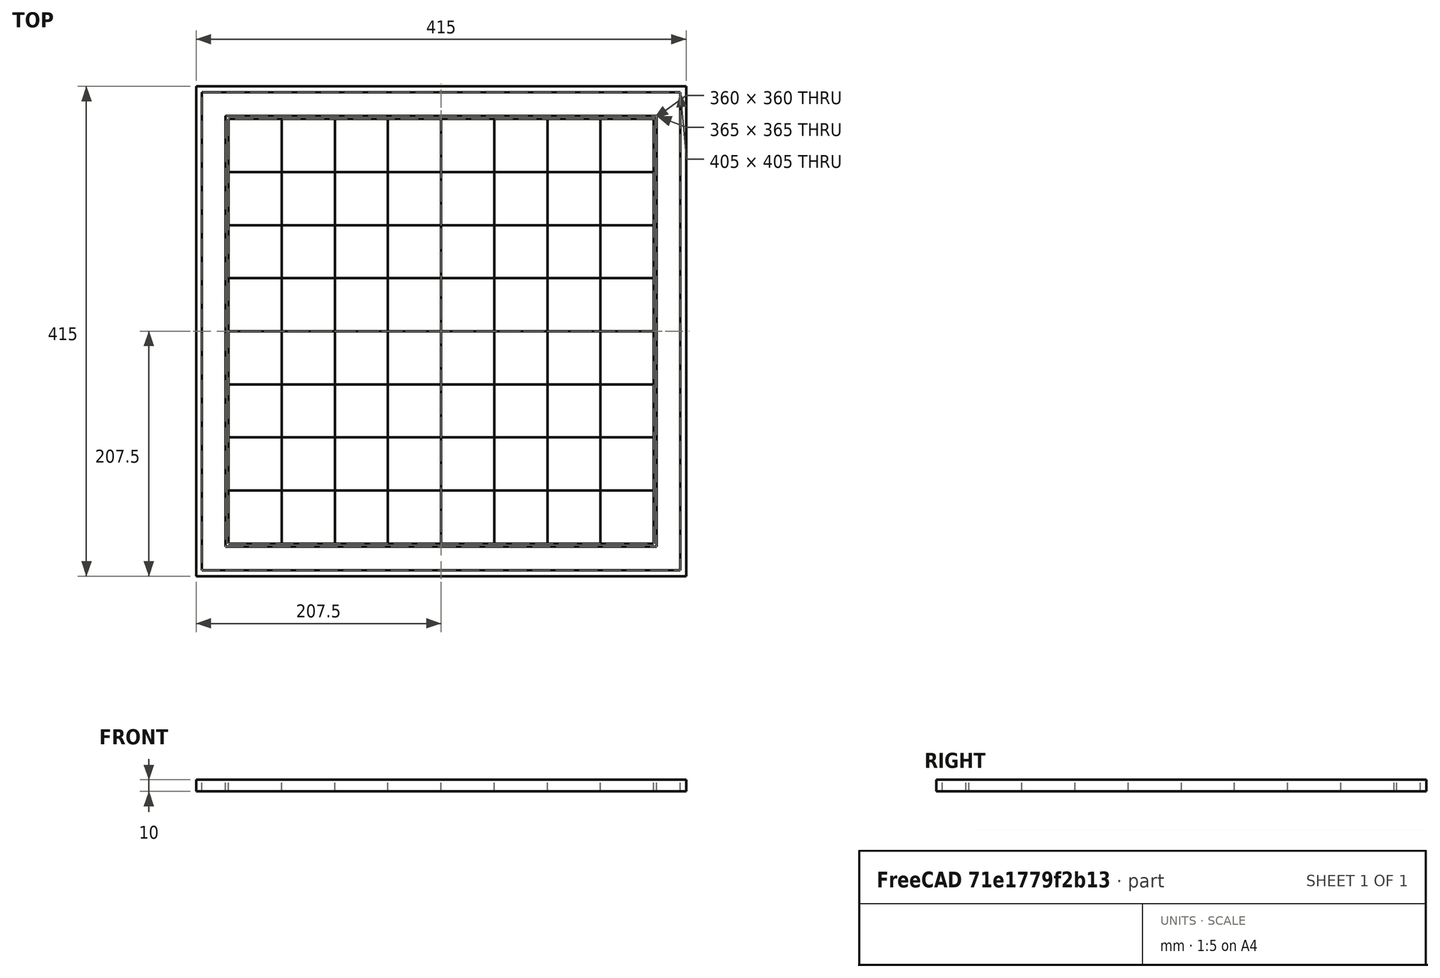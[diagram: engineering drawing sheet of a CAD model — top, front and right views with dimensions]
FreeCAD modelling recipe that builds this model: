
FCSTD DOCUMENT  (FreeCAD 0.20R29410 (Git))
Label: checkersWithCrowns
License: All rights reserved
LicenseURL: http://en.wikipedia.org/wiki/All_rights_reserved
objects: Part::Box×66, Mesh::Feature×48, App::DocumentObjectGroup×13, Sketcher::SketchObject×2, Part::Extrusion×2, Part::Cut×1
note: 71 computed .brp shape members not serialized (recipe doc carries the construction recipe); baked Part::Feature solids carry a one-line shape summary decoded from their .brp

FEATURE [Part::Box] Box  label="A1"
  AttacherType = Attacher::AttachEngine3D
  Height = 10
  Length = 45
  Width = 45
FEATURE [Part::Box] Box001  label="A2"
  AttacherType = Attacher::AttachEngine3D
  Height = 10
  Length = 45
  Placement = pos=(45,0,0) rot=(0,0,1;0rad)
  Width = 45
FEATURE [Part::Box] Box002  label="A3"
  AttacherType = Attacher::AttachEngine3D
  Height = 10
  Length = 45
  Placement = pos=(90,0,0) rot=(0,0,1;0rad)
  Width = 45
FEATURE [Part::Box] Box003  label="A4"
  AttacherType = Attacher::AttachEngine3D
  Height = 10
  Length = 45
  Placement = pos=(135,0,0) rot=(0,0,1;0rad)
  Width = 45
FEATURE [Part::Box] Box004  label="A5"
  AttacherType = Attacher::AttachEngine3D
  Height = 10
  Length = 45
  Placement = pos=(180,0,0) rot=(0,0,1;0rad)
  Width = 45
FEATURE [Part::Box] Box005  label="A6"
  AttacherType = Attacher::AttachEngine3D
  Height = 10
  Length = 45
  Placement = pos=(225,0,0) rot=(0,0,1;0rad)
  Width = 45
FEATURE [Part::Box] Box006  label="A7"
  AttacherType = Attacher::AttachEngine3D
  Height = 10
  Length = 45
  Placement = pos=(270,0,0) rot=(0,0,1;0rad)
  Width = 45
FEATURE [Part::Box] Box007  label="A8"
  AttacherType = Attacher::AttachEngine3D
  Height = 10
  Length = 45
  Placement = pos=(315,0,0) rot=(0,0,1;0rad)
  Width = 45
FEATURE [App::DocumentObjectGroup] Group001  label="A_File"
  Group = -> [Box,Box001,Box002,Box003,Box004,Box005,Box006,Box007]
FEATURE [Part::Box] Box008  label="B1"
  AttacherType = Attacher::AttachEngine3D
  Height = 10
  Length = 45
  Placement = pos=(0,45,0) rot=(0,0,1;0rad)
  Width = 45
FEATURE [Part::Box] Box009  label="B2"
  AttacherType = Attacher::AttachEngine3D
  Height = 10
  Length = 45
  Placement = pos=(45,45,0) rot=(0,0,1;0rad)
  Width = 45
FEATURE [Part::Box] Box010  label="B3"
  AttacherType = Attacher::AttachEngine3D
  Height = 10
  Length = 45
  Placement = pos=(90,45,0) rot=(0,0,1;0rad)
  Width = 45
FEATURE [Part::Box] Box011  label="B4"
  AttacherType = Attacher::AttachEngine3D
  Height = 10
  Length = 45
  Placement = pos=(135,45,0) rot=(0,0,1;0rad)
  Width = 45
FEATURE [Part::Box] Box012  label="B5"
  AttacherType = Attacher::AttachEngine3D
  Height = 10
  Length = 45
  Placement = pos=(180,45,0) rot=(0,0,1;0rad)
  Width = 45
FEATURE [Part::Box] Box013  label="B6"
  AttacherType = Attacher::AttachEngine3D
  Height = 10
  Length = 45
  Placement = pos=(225,45,0) rot=(0,0,1;0rad)
  Width = 45
FEATURE [Part::Box] Box014  label="B7"
  AttacherType = Attacher::AttachEngine3D
  Height = 10
  Length = 45
  Placement = pos=(270,45,0) rot=(0,0,1;0rad)
  Width = 45
FEATURE [Part::Box] Box015  label="B8"
  AttacherType = Attacher::AttachEngine3D
  Height = 10
  Length = 45
  Placement = pos=(315,45,0) rot=(0,0,1;0rad)
  Width = 45
FEATURE [Part::Box] Box016  label="C8"
  AttacherType = Attacher::AttachEngine3D
  Height = 10
  Length = 45
  Placement = pos=(315,90,0) rot=(0,0,1;0rad)
  Width = 45
FEATURE [Part::Box] Box017  label="C7"
  AttacherType = Attacher::AttachEngine3D
  Height = 10
  Length = 45
  Placement = pos=(270,90,0) rot=(0,0,1;0rad)
  Width = 45
FEATURE [Part::Box] Box018  label="C6"
  AttacherType = Attacher::AttachEngine3D
  Height = 10
  Length = 45
  Placement = pos=(225,90,0) rot=(0,0,1;0rad)
  Width = 45
FEATURE [Part::Box] Box019  label="C5"
  AttacherType = Attacher::AttachEngine3D
  Height = 10
  Length = 45
  Placement = pos=(180,90,0) rot=(0,0,1;0rad)
  Width = 45
FEATURE [Part::Box] Box020  label="C4"
  AttacherType = Attacher::AttachEngine3D
  Height = 10
  Length = 45
  Placement = pos=(135,90,0) rot=(0,0,1;0rad)
  Width = 45
FEATURE [Part::Box] Box021  label="C3"
  AttacherType = Attacher::AttachEngine3D
  Height = 10
  Length = 45
  Placement = pos=(90,90,0) rot=(0,0,1;0rad)
  Width = 45
FEATURE [Part::Box] Box022  label="C2"
  AttacherType = Attacher::AttachEngine3D
  Height = 10
  Length = 45
  Placement = pos=(45,90,0) rot=(0,0,1;0rad)
  Width = 45
FEATURE [Part::Box] Box023  label="C1"
  AttacherType = Attacher::AttachEngine3D
  Height = 10
  Length = 45
  Placement = pos=(0,90,0) rot=(0,0,1;0rad)
  Width = 45
FEATURE [App::DocumentObjectGroup] Group002  label="B_File"
  Group = -> [Box008,Box009,Box010,Box011,Box012,Box013,Box014,Box015]
FEATURE [App::DocumentObjectGroup] Group003  label="C_File"
  Group = -> [Box016,Box017,Box018,Box019,Box020,Box021,Box022,Box023]
FEATURE [Part::Box] Box024  label="D8"
  AttacherType = Attacher::AttachEngine3D
  Height = 10
  Length = 45
  Placement = pos=(315,135,0) rot=(0,0,1;0rad)
  Width = 45
FEATURE [Part::Box] Box025  label="D7"
  AttacherType = Attacher::AttachEngine3D
  Height = 10
  Length = 45
  Placement = pos=(270,135,0) rot=(0,0,1;0rad)
  Width = 45
FEATURE [Part::Box] Box026  label="D6"
  AttacherType = Attacher::AttachEngine3D
  Height = 10
  Length = 45
  Placement = pos=(225,135,0) rot=(0,0,1;0rad)
  Width = 45
FEATURE [Part::Box] Box027  label="D5"
  AttacherType = Attacher::AttachEngine3D
  Height = 10
  Length = 45
  Placement = pos=(180,135,0) rot=(0,0,1;0rad)
  Width = 45
FEATURE [Part::Box] Box028  label="D4"
  AttacherType = Attacher::AttachEngine3D
  Height = 10
  Length = 45
  Placement = pos=(135,135,0) rot=(0,0,1;0rad)
  Width = 45
FEATURE [Part::Box] Box029  label="D3"
  AttacherType = Attacher::AttachEngine3D
  Height = 10
  Length = 45
  Placement = pos=(90,135,0) rot=(0,0,1;0rad)
  Width = 45
FEATURE [Part::Box] Box030  label="D2"
  AttacherType = Attacher::AttachEngine3D
  Height = 10
  Length = 45
  Placement = pos=(45,135,0) rot=(0,0,1;0rad)
  Width = 45
FEATURE [Part::Box] Box031  label="D1"
  AttacherType = Attacher::AttachEngine3D
  Height = 10
  Length = 45
  Placement = pos=(0,135,0) rot=(0,0,1;0rad)
  Width = 45
FEATURE [Part::Box] Box032  label="E8"
  AttacherType = Attacher::AttachEngine3D
  Height = 10
  Length = 45
  Placement = pos=(315,180,0) rot=(0,0,1;0rad)
  Width = 45
FEATURE [Part::Box] Box033  label="E7"
  AttacherType = Attacher::AttachEngine3D
  Height = 10
  Length = 45
  Placement = pos=(270,180,0) rot=(0,0,1;0rad)
  Width = 45
FEATURE [Part::Box] Box034  label="E6"
  AttacherType = Attacher::AttachEngine3D
  Height = 10
  Length = 45
  Placement = pos=(225,180,0) rot=(0,0,1;0rad)
  Width = 45
FEATURE [Part::Box] Box035  label="E5"
  AttacherType = Attacher::AttachEngine3D
  Height = 10
  Length = 45
  Placement = pos=(180,180,0) rot=(0,0,1;0rad)
  Width = 45
FEATURE [Part::Box] Box036  label="E4"
  AttacherType = Attacher::AttachEngine3D
  Height = 10
  Length = 45
  Placement = pos=(135,180,0) rot=(0,0,1;0rad)
  Width = 45
FEATURE [Part::Box] Box037  label="E3"
  AttacherType = Attacher::AttachEngine3D
  Height = 10
  Length = 45
  Placement = pos=(90,180,0) rot=(0,0,1;0rad)
  Width = 45
FEATURE [Part::Box] Box038  label="E2"
  AttacherType = Attacher::AttachEngine3D
  Height = 10
  Length = 45
  Placement = pos=(45,180,0) rot=(0,0,1;0rad)
  Width = 45
FEATURE [Part::Box] Box039  label="E1"
  AttacherType = Attacher::AttachEngine3D
  Height = 10
  Length = 45
  Placement = pos=(0,180,0) rot=(0,0,1;0rad)
  Width = 45
FEATURE [App::DocumentObjectGroup] Group004  label="D_File"
  Group = -> [Box024,Box025,Box026,Box027,Box028,Box029,Box030,Box031]
FEATURE [Part::Box] Box040  label="F1"
  AttacherType = Attacher::AttachEngine3D
  Height = 10
  Length = 45
  Placement = pos=(0,225,0) rot=(0,0,1;0rad)
  Width = 45
FEATURE [Part::Box] Box041  label="F2"
  AttacherType = Attacher::AttachEngine3D
  Height = 10
  Length = 45
  Placement = pos=(45,225,0) rot=(0,0,1;0rad)
  Width = 45
FEATURE [Part::Box] Box042  label="F3"
  AttacherType = Attacher::AttachEngine3D
  Height = 10
  Length = 45
  Placement = pos=(90,225,0) rot=(0,0,1;0rad)
  Width = 45
FEATURE [Part::Box] Box043  label="F4"
  AttacherType = Attacher::AttachEngine3D
  Height = 10
  Length = 45
  Placement = pos=(135,225,0) rot=(0,0,1;0rad)
  Width = 45
FEATURE [Part::Box] Box044  label="F5"
  AttacherType = Attacher::AttachEngine3D
  Height = 10
  Length = 45
  Placement = pos=(180,225,0) rot=(0,0,1;0rad)
  Width = 45
FEATURE [Part::Box] Box045  label="F6"
  AttacherType = Attacher::AttachEngine3D
  Height = 10
  Length = 45
  Placement = pos=(225,225,0) rot=(0,0,1;0rad)
  Width = 45
FEATURE [Part::Box] Box046  label="F7"
  AttacherType = Attacher::AttachEngine3D
  Height = 10
  Length = 45
  Placement = pos=(270,225,0) rot=(0,0,1;0rad)
  Width = 45
FEATURE [Part::Box] Box047  label="F8"
  AttacherType = Attacher::AttachEngine3D
  Height = 10
  Length = 45
  Placement = pos=(315,225,0) rot=(0,0,1;0rad)
  Width = 45
FEATURE [App::DocumentObjectGroup] Group005  label="E_File"
  Group = -> [Box032,Box033,Box034,Box035,Box036,Box037,Box038,Box039]
FEATURE [Part::Box] Box048  label="G8"
  AttacherType = Attacher::AttachEngine3D
  Height = 10
  Length = 45
  Placement = pos=(315,270,0) rot=(0,0,1;0rad)
  Width = 45
FEATURE [Part::Box] Box049  label="G1"
  AttacherType = Attacher::AttachEngine3D
  Height = 10
  Length = 45
  Placement = pos=(0,270,0) rot=(0,0,1;0rad)
  Width = 45
FEATURE [Part::Box] Box050  label="G2"
  AttacherType = Attacher::AttachEngine3D
  Height = 10
  Length = 45
  Placement = pos=(45,270,0) rot=(0,0,1;0rad)
  Width = 45
FEATURE [Part::Box] Box051  label="G3"
  AttacherType = Attacher::AttachEngine3D
  Height = 10
  Length = 45
  Placement = pos=(90,270,0) rot=(0,0,1;0rad)
  Width = 45
FEATURE [Part::Box] Box052  label="G4"
  AttacherType = Attacher::AttachEngine3D
  Height = 10
  Length = 45
  Placement = pos=(135,270,0) rot=(0,0,1;0rad)
  Width = 45
FEATURE [Part::Box] Box053  label="G5"
  AttacherType = Attacher::AttachEngine3D
  Height = 10
  Length = 45
  Placement = pos=(180,270,0) rot=(0,0,1;0rad)
  Width = 45
FEATURE [Part::Box] Box054  label="G6"
  AttacherType = Attacher::AttachEngine3D
  Height = 10
  Length = 45
  Placement = pos=(225,270,0) rot=(0,0,1;0rad)
  Width = 45
FEATURE [Part::Box] Box055  label="G7"
  AttacherType = Attacher::AttachEngine3D
  Height = 10
  Length = 45
  Placement = pos=(270,270,0) rot=(0,0,1;0rad)
  Width = 45
FEATURE [App::DocumentObjectGroup] Group006  label="F_File"
  Group = -> [Box040,Box041,Box042,Box043,Box044,Box045,Box046,Box047]
FEATURE [Part::Box] Box056  label="H7"
  AttacherType = Attacher::AttachEngine3D
  Height = 10
  Length = 45
  Placement = pos=(270,315,0) rot=(0,0,1;0rad)
  Width = 45
FEATURE [Part::Box] Box057  label="H6"
  AttacherType = Attacher::AttachEngine3D
  Height = 10
  Length = 45
  Placement = pos=(225,315,0) rot=(0,0,1;0rad)
  Width = 45
FEATURE [Part::Box] Box058  label="H5"
  AttacherType = Attacher::AttachEngine3D
  Height = 10
  Length = 45
  Placement = pos=(180,315,0) rot=(0,0,1;0rad)
  Width = 45
FEATURE [Part::Box] Box059  label="H4"
  AttacherType = Attacher::AttachEngine3D
  Height = 10
  Length = 45
  Placement = pos=(135,315,0) rot=(0,0,1;0rad)
  Width = 45
FEATURE [Part::Box] Box060  label="H3"
  AttacherType = Attacher::AttachEngine3D
  Height = 10
  Length = 45
  Placement = pos=(90,315,0) rot=(0,0,1;0rad)
  Width = 45
FEATURE [Part::Box] Box061  label="H2"
  AttacherType = Attacher::AttachEngine3D
  Height = 10
  Length = 45
  Placement = pos=(45,315,0) rot=(0,0,1;0rad)
  Width = 45
FEATURE [Part::Box] Box062  label="H1"
  AttacherType = Attacher::AttachEngine3D
  Height = 10
  Length = 45
  Placement = pos=(0,315,0) rot=(0,0,1;0rad)
  Width = 45
FEATURE [Part::Box] Box063  label="H8"
  AttacherType = Attacher::AttachEngine3D
  Height = 10
  Length = 45
  Placement = pos=(315,315,0) rot=(0,0,1;0rad)
  Width = 45
FEATURE [App::DocumentObjectGroup] Group007  label="G_File"
  Group = -> [Box048,Box049,Box050,Box051,Box052,Box053,Box054,Box055]
FEATURE [App::DocumentObjectGroup] Group008  label="H_File"
  Group = -> [Box056,Box057,Box058,Box059,Box060,Box061,Box062,Box063]
FEATURE [Part::Box] Box064  label="Cube"
  AttacherType = Attacher::AttachEngine3D
  Height = 10
  Length = 365
  Width = 365
FEATURE [Part::Box] Box065  label="Cube001"
  AttacherType = Attacher::AttachEngine3D
  Height = 10
  Length = 360
  Placement = pos=(2.5,2.5,0) rot=(0,0,1;0rad)
  Width = 360
FEATURE [Part::Cut] Cut
  Base = -> Box064
  Placement = pos=(-2.5,-2.5,0) rot=(0,0,1;0rad)
  Tool = -> Box065
FEATURE [Sketcher::SketchObject] Sketch
  FullyConstrained = true
  MapMode = 2
  Support = -> [Box064]
  sketch-geometry (8):
    g0: LineSegment StartX=0 StartY=0 StartZ=0 EndX=405 EndY=0 EndZ=0
    g1: LineSegment StartX=405 StartY=0 StartZ=0 EndX=405 EndY=405 EndZ=0
    g2: LineSegment StartX=405 StartY=405 StartZ=0 EndX=0 EndY=405 EndZ=0
    g3: LineSegment StartX=0 StartY=405 StartZ=0 EndX=0 EndY=0 EndZ=0
    g4: LineSegment StartX=20 StartY=20 StartZ=0 EndX=385 EndY=20 EndZ=0
    g5: LineSegment StartX=385 StartY=20 StartZ=0 EndX=385 EndY=385 EndZ=0
    g6: LineSegment StartX=385 StartY=385 StartZ=0 EndX=20 EndY=385 EndZ=0
    g7: LineSegment StartX=20 StartY=385 StartZ=0 EndX=20 EndY=20 EndZ=0
  constraints (24):
    c: Coincident(g0,g1)
    c: Coincident(g1,g2)
    c: Coincident(g2,g3)
    c: Coincident(g3,g0)
    c: Horizontal(g0)
    c: Horizontal(g2)
    c: Vertical(g1)
    c: Vertical(g3)
    c: PointOnObject(g0,g-1)
    c: Coincident(g4,g5)
    c: Coincident(g5,g6)
    c: Coincident(g6,g7)
    c: Coincident(g7,g4)
    c: Horizontal(g4)
    c: Horizontal(g6)
    c: Vertical(g5)
    c: Vertical(g7)
    c: DistanceX(g5,g1) = 20
    c: DistanceX(g2,g6) = 20
    c: DistanceY(g0,g4) = 20
    c: DistanceY(g6,g2) = 20
    c: DistanceY(g0,g1) = 405
    c: DistanceX(g0,g0) = 405
    c: DistanceX(g-1,g0) = 0
FEATURE [Part::Extrusion] Extrude
  Base = -> Sketch
  Dir = (0,0,1)
  DirMode = 2
  FaceMakerClass = Part::FaceMakerBullseye
  LengthFwd = 10
  LengthRev = 0
  Placement = pos=(-22.5,-22.5,0) rot=(0,0,1;0rad)
  Solid = true
  Symmetric = false
FEATURE [Sketcher::SketchObject] Sketch001
  FullyConstrained = true
  sketch-geometry (8):
    g0: LineSegment StartX=5 StartY=5 StartZ=0 EndX=410 EndY=5 EndZ=0
    g1: LineSegment StartX=410 StartY=5 StartZ=0 EndX=410 EndY=410 EndZ=0
    g2: LineSegment StartX=410 StartY=410 StartZ=0 EndX=5 EndY=410 EndZ=0
    g3: LineSegment StartX=5 StartY=410 StartZ=0 EndX=5 EndY=5 EndZ=0
    g4: LineSegment StartX=0 StartY=0 StartZ=0 EndX=415 EndY=0 EndZ=0
    g5: LineSegment StartX=415 StartY=0 StartZ=0 EndX=415 EndY=415 EndZ=0
    g6: LineSegment StartX=415 StartY=415 StartZ=0 EndX=0 EndY=415 EndZ=0
    g7: LineSegment StartX=0 StartY=415 StartZ=0 EndX=0 EndY=0 EndZ=0
  constraints (24):
    c: Coincident(g0,g1)
    c: Coincident(g1,g2)
    c: Coincident(g2,g3)
    c: Coincident(g3,g0)
    c: Horizontal(g0)
    c: Horizontal(g2)
    c: Vertical(g1)
    c: Vertical(g3)
    c: Coincident(g4,g5)
    c: Coincident(g5,g6)
    c: Coincident(g6,g7)
    c: Coincident(g7,g4)
    c: Horizontal(g4)
    c: Horizontal(g6)
    c: Vertical(g5)
    c: Vertical(g7)
    c: DistanceX(g4,g0) = 5
    c: DistanceX(g0,g4) = 5
    c: DistanceY(g1,g5) = 5
    c: DistanceY(g4,g0) = 5
    c: DistanceY(g4,g5) = 415
    c: DistanceX(g6,g5) = 415
    c: DistanceX(g4,g-1) = 0
    c: DistanceY(g4,g-1) = 0
FEATURE [Part::Extrusion] Extrude001
  Base = -> Sketch001
  Dir = (0,0,1)
  DirMode = 2
  FaceMakerClass = Part::FaceMakerBullseye
  LengthFwd = 10
  LengthRev = 0
  Placement = pos=(-27.5,-27.5,0) rot=(0,0,1;0rad)
  Solid = true
  Symmetric = false
FEATURE [App::DocumentObjectGroup] Group  label="Board"
  Group = -> [Group001,Group002,Group003,Group004,Group005,Group006,Group007,Group008,Cut,Extrude,Extrude001]
FEATURE [Mesh::Feature] checkers_Black01  label="Black01"
FEATURE [Mesh::Feature] checkers_White01  label="White01"
FEATURE [Mesh::Feature] checkers_White002  label="White02"
  Placement = pos=(90,0,0) rot=(0,0,1;0rad)
FEATURE [Mesh::Feature] checkers_White003  label="White03"
  Placement = pos=(180,0,0) rot=(0,0,1;0rad)
FEATURE [Mesh::Feature] checkers_White004  label="White04"
  Placement = pos=(270,0,0) rot=(0,0,1;0rad)
FEATURE [Mesh::Feature] checkers_White005  label="White05"
  Placement = pos=(45,45,0) rot=(0,0,1;0rad)
FEATURE [Mesh::Feature] checkers_White006  label="White06"
  Placement = pos=(135,45,0) rot=(0,0,1;0rad)
FEATURE [Mesh::Feature] checkers_White007  label="White07"
  Placement = pos=(225,45,0) rot=(0,0,1;0rad)
FEATURE [Mesh::Feature] checkers_White008  label="White08"
  Placement = pos=(315,45,0) rot=(0,0,1;0rad)
FEATURE [Mesh::Feature] checkers_White009  label="White09"
  Placement = pos=(0,90,0) rot=(0,0,1;0rad)
FEATURE [Mesh::Feature] checkers_White010  label="White10"
  Placement = pos=(90,90,0) rot=(0,0,1;0rad)
FEATURE [Mesh::Feature] checkers_White011  label="White11"
  Placement = pos=(180,90,0) rot=(0,0,1;0rad)
FEATURE [Mesh::Feature] checkers_White012  label="White12"
  Placement = pos=(270,90,0) rot=(0,0,1;0rad)
FEATURE [Mesh::Feature] checkers_Black002  label="Black02"
  Placement = pos=(-90,0,0) rot=(0,0,1;0rad)
FEATURE [Mesh::Feature] checkers_Black003  label="Black03"
  Placement = pos=(-180,0,0) rot=(0,0,1;0rad)
FEATURE [Mesh::Feature] checkers_Black004  label="Black04"
  Placement = pos=(-270,0,0) rot=(0,0,1;0rad)
FEATURE [Mesh::Feature] checkers_Black005  label="Black05"
  Placement = pos=(-45,-45,0) rot=(0,0,1;0rad)
FEATURE [Mesh::Feature] checkers_Black006  label="Black06"
  Placement = pos=(-135,-45,0) rot=(0,0,1;0rad)
FEATURE [Mesh::Feature] checkers_Black007  label="Black07"
  Placement = pos=(-225,-45,0) rot=(0,0,1;0rad)
FEATURE [Mesh::Feature] checkers_Black008  label="Black08"
  Placement = pos=(-315,-45,0) rot=(0,0,1;0rad)
FEATURE [Mesh::Feature] checkers_Black009  label="Black09"
  Placement = pos=(0,-90,0) rot=(0,0,1;0rad)
FEATURE [Mesh::Feature] checkers_Black010  label="Black10"
  Placement = pos=(-90,-90,0) rot=(0,0,1;0rad)
FEATURE [Mesh::Feature] checkers_Black011  label="Black11"
  Placement = pos=(-180,-90,0) rot=(0,0,1;0rad)
FEATURE [Mesh::Feature] checkers_Black012  label="Black12"
  Placement = pos=(-270,-90,0) rot=(0,0,1;0rad)
FEATURE [App::DocumentObjectGroup] Group009  label="Black"
  Group = -> [checkers_Black002,checkers_Black003,checkers_Black004,checkers_Black005,checkers_Black006,checkers_Black007,checkers_Black008,checkers_Black009,checkers_Black010,checkers_Black011,checkers_Black012,checkers_Black01]
FEATURE [App::DocumentObjectGroup] Group010  label="White"
  Group = -> [checkers_White01,checkers_White002,checkers_White003,checkers_White004,checkers_White005,checkers_White006,checkers_White007,checkers_White008,checkers_White009,checkers_White010,checkers_White011,checkers_White012]
FEATURE [Mesh::Feature] blackCrown  label="blackCrown1"
FEATURE [Mesh::Feature] blackCrown001  label="blackCrown2"
  Placement = pos=(-90,0,0) rot=(0,0,1;0rad)
FEATURE [Mesh::Feature] blackCrown002  label="blackCrown3"
  Placement = pos=(-180,0,0) rot=(0,0,1;0rad)
FEATURE [Mesh::Feature] blackCrown003  label="blackCrown4"
  Placement = pos=(-270,0,0) rot=(0,0,1;0rad)
FEATURE [Mesh::Feature] blackCrown004  label="blackCrown5"
  Placement = pos=(-45,-45,0) rot=(0,0,1;0rad)
FEATURE [Mesh::Feature] blackCrown005  label="blackCrown6"
  Placement = pos=(-135,-45,0) rot=(0,0,1;0rad)
FEATURE [Mesh::Feature] blackCrown006  label="blackCrown7"
  Placement = pos=(-225,-45,0) rot=(0,0,1;0rad)
FEATURE [Mesh::Feature] blackCrown007  label="blackCrown8"
  Placement = pos=(-315,-45,0) rot=(0,0,1;0rad)
FEATURE [Mesh::Feature] blackCrown008  label="blackCrown9"
  Placement = pos=(0,-90,0) rot=(0,0,1;0rad)
FEATURE [Mesh::Feature] blackCrown009  label="blackCrown10"
  Placement = pos=(-90,-90,0) rot=(0,0,1;0rad)
FEATURE [Mesh::Feature] blackCrown010  label="blackCrown11"
  Placement = pos=(-180,-90,0) rot=(0,0,1;0rad)
FEATURE [Mesh::Feature] blackCrown011  label="blackCrown12"
  Placement = pos=(-270,-90,0) rot=(0,0,1;0rad)
FEATURE [App::DocumentObjectGroup] Group011  label="BlackCrowns"
  Group = -> [blackCrown,blackCrown001,blackCrown002,blackCrown003,blackCrown004,blackCrown005,blackCrown006,blackCrown007,blackCrown008,blackCrown009,blackCrown010,blackCrown011]
FEATURE [Mesh::Feature] whiteCrown  label="whiteCrown1"
FEATURE [Mesh::Feature] whiteCrown001  label="whiteCrown2"
  Placement = pos=(90,0,0) rot=(0,0,1;0rad)
FEATURE [Mesh::Feature] whiteCrown002  label="whiteCrown3"
  Placement = pos=(180,0,0) rot=(0,0,1;0rad)
FEATURE [Mesh::Feature] whiteCrown003  label="whiteCrown4"
  Placement = pos=(270,0,0) rot=(0,0,1;0rad)
FEATURE [Mesh::Feature] whiteCrown004  label="whiteCrown5"
  Placement = pos=(45,45,0) rot=(0,0,1;0rad)
FEATURE [Mesh::Feature] whiteCrown005  label="whiteCrown6"
  Placement = pos=(135,45,0) rot=(0,0,1;0rad)
FEATURE [Mesh::Feature] whiteCrown006  label="whiteCrown7"
  Placement = pos=(225,45,0) rot=(0,0,1;0rad)
FEATURE [Mesh::Feature] whiteCrown007  label="whiteCrown8"
  Placement = pos=(315,45,0) rot=(0,0,1;0rad)
FEATURE [Mesh::Feature] whiteCrown008  label="whiteCrown9"
  Placement = pos=(0,90,0) rot=(0,0,1;0rad)
FEATURE [Mesh::Feature] whiteCrown009  label="whiteCrown10"
  Placement = pos=(90,90,0) rot=(0,0,1;0rad)
FEATURE [Mesh::Feature] whiteCrown010  label="whiteCrown11"
  Placement = pos=(180,90,0) rot=(0,0,1;0rad)
FEATURE [Mesh::Feature] whiteCrown011  label="whiteCrown12"
  Placement = pos=(270,90,0) rot=(0,0,1;0rad)
FEATURE [App::DocumentObjectGroup] Group012  label="WhiteCrowns"
  Group = -> [whiteCrown,whiteCrown001,whiteCrown002,whiteCrown003,whiteCrown004,whiteCrown005,whiteCrown006,whiteCrown007,whiteCrown008,whiteCrown009,whiteCrown010,whiteCrown011]
